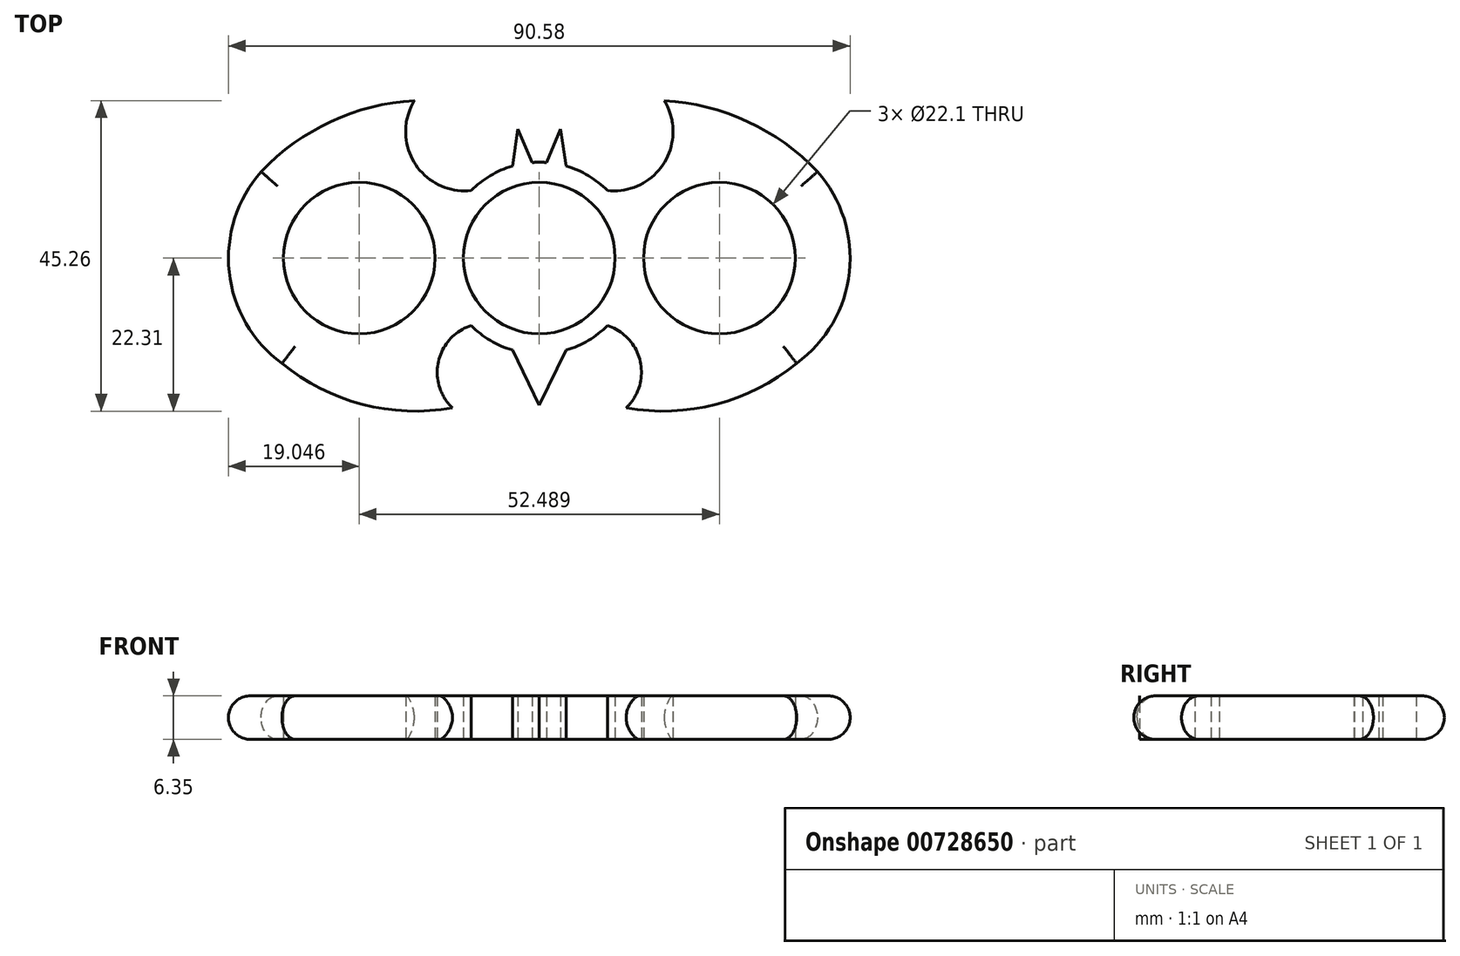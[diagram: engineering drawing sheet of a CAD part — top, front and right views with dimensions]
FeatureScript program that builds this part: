
annotation { "Feature Type Name" : "Feature", "Feature Type Description" : "" }
export const myFeature = defineFeature(function(context is Context, id is Id, definition is map)
    precondition{}
    {
        {
            var Q0;
            Q0=qCreatedBy(makeId("Top.planeOp"),FACE);
            var sketch = newSketch(context, id + "F0", { "sketchPlane" : qUnion([Q0])});
            skCircle(sketch, "E0", {"center": v(0, 0) * mm, "radius": 11.05 * mm});
            skCircle(sketch, "E1", {"center": v(0, 0) * mm, "radius": 13.97 * mm});
            skLineSegment(sketch, "E2", {"start": v(0, 0) * mm, "end": v(-26.24, 0) * mm});
            skCircle(sketch, "E3", {"center": v(-26.24, 0) * mm, "radius": 11.05 * mm});
            skLineSegment(sketch, "E4", {"start": v(0, 0) * mm, "end": v(26.24, 0) * mm});
            skCircle(sketch, "E5", {"center": v(26.24, 0) * mm, "radius": 11.05 * mm});
            skArc(sketch, "E6", {"start": v(37.5, -15.37) * mm, "mid": v(45.18, -2.05) * mm, "end": v(40.53, 12.6) * mm});
            skArc(sketch, "E7", {"start": v(-18.2, 22.95) * mm, "mid": v(-30.36, 19.9) * mm, "end": v(-40.53, 12.6) * mm});
            skArc(sketch, "E8", {"start": v(-18.2, 22.95) * mm, "mid": v(-18.15, 13.81) * mm, "end": v(-9.93, 9.83) * mm});
            skArc(sketch, "E9.trimOffspring", {"start": v(-40.53, 12.6) * mm, "mid": v(-45.18, -2.05) * mm, "end": v(-37.5, -15.37) * mm});
            skArc(sketch, "E10.MirrorCS", {"start": v(18.2, 22.95) * mm, "mid": v(18.15, 13.81) * mm, "end": v(9.93, 9.83) * mm});
            skArc(sketch, "E11.MirrorCS", {"start": v(18.2, 22.95) * mm, "mid": v(30.36, 19.9) * mm, "end": v(40.53, 12.6) * mm});
            skArc(sketch, "E12", {"start": v(-37.5, -15.37) * mm, "mid": v(-25.79, -21.32) * mm, "end": v(-12.65, -21.85) * mm});
            skArc(sketch, "E13", {"start": v(-9.93, -9.83) * mm, "mid": v(-14.7, -15.06) * mm, "end": v(-12.65, -21.85) * mm});
            skArc(sketch, "E14.MirrorCS", {"start": v(9.93, -9.83) * mm, "mid": v(14.7, -15.06) * mm, "end": v(12.65, -21.85) * mm});
            skArc(sketch, "E15.MirrorCS", {"start": v(37.5, -15.37) * mm, "mid": v(25.79, -21.32) * mm, "end": v(12.65, -21.85) * mm});
            skPoint(sketch, "E16.end.orphan", {"position": v(2.34, 18.82) * mm});
            skPoint(sketch, "E17.orphan", {"position": v(3.92, 13.4) * mm});
            skPoint(sketch, "E18.end.orphan", {"position": v(-1.04, 13.93) * mm});
            skPoint(sketch, "E19.end.orphan", {"position": v(-2.23, 18.82) * mm});
            skPoint(sketch, "E20.MirrorCS.end.orphan", {"position": v(1.04, 13.93) * mm});
            skPoint(sketch, "E20.MirrorCS.start.orphan", {"position": v(2.23, 18.82) * mm});
            skPoint(sketch, "E21.end.orphan", {"position": v(-4.8, 18.35) * mm});
            skPoint(sketch, "E22.MirrorCS.end.orphan", {"position": v(4.8, 18.35) * mm});
            skLineSegment(sketch, "E23", {"start": v(-1.04, 13.93) * mm, "end": v(-3.1, 18.83) * mm});
            skLineSegment(sketch, "E24", {"start": v(-3.1, 18.83) * mm, "end": v(-3.92, 13.4) * mm});
            skLineSegment(sketch, "E25.MirrorCS", {"start": v(1.04, 13.93) * mm, "end": v(3.1, 18.83) * mm});
            skLineSegment(sketch, "E26.MirrorCS", {"start": v(3.1, 18.83) * mm, "end": v(3.92, 13.4) * mm});
            skPoint(sketch, "E27.end.orphan", {"position": v(0, -21.45) * mm});
            skPoint(sketch, "E27.start.orphan", {"position": v(-4.01, -13.38) * mm});
            skPoint(sketch, "E28.MirrorCS.start.orphan", {"position": v(4.01, -13.38) * mm});
            skPoint(sketch, "E29.MirrorCS.end.orphan", {"position": v(-3.92, -13.4) * mm});
            skPoint(sketch, "E29.MirrorCS.start.orphan", {"position": v(-3.1, -18.83) * mm});
            skLineSegment(sketch, "E30", {"start": v(-3.92, -13.4) * mm, "end": v(0, -21.45) * mm});
            skLineSegment(sketch, "E31.MirrorCS", {"start": v(3.92, -13.4) * mm, "end": v(0, -21.45) * mm});
            skSolve(sketch);
        }
        {
            var Q0;
            Q0=qSketchRegion(id+"F0",true);
            extrude(context, id + "F1", {"entities" : qUnion([Q0]), "depth" : 6.35 * mm, "offsetDistance" : 25.4 * mm});
        }
        {
            var Q0;
            Q0=makeQuery(id+"F1.opExtrude","CAP_EDGE",EDGE,{"disambiguationData":[OSD([sQuery(id+"F0.wireOp",EDGE,"E9.trimOffspring")])],"isStart":false});
            var Q1;
            Q1=makeQuery(id+"F1.opExtrude","CAP_EDGE",EDGE,{"disambiguationData":[OSD([sQuery(id+"F0.wireOp",EDGE,"E6")])],"isStart":false});
            var Q2;
            Q2=makeQuery(id+"F1.opExtrude","CAP_EDGE",EDGE,{"disambiguationData":[OSD([sQuery(id+"F0.wireOp",EDGE,"E6")])],"isStart":true});
            var Q3;
            Q3=makeQuery(id+"F1.opExtrude","CAP_EDGE",EDGE,{"disambiguationData":[OSD([sQuery(id+"F0.wireOp",EDGE,"E9.trimOffspring")])],"isStart":true});
            fillet(context, id + "F2", {"entities" : qUnion([Q0, Q1, Q2, Q3]), "radius" : 3.17 * mm, "tangentPropagation" : true, "allowEdgeOverflow" : false});
        }
    });
